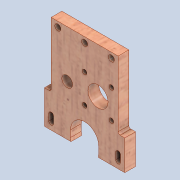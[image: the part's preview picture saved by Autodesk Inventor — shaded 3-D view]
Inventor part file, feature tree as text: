
AUTODESK INVENTOR PART (.ipt)
format: ipt  version: 2020 (Build 240168000, 168)  size: 326,656 bytes
history: native  units: mm
features: extrude x6, sketch x4, other x3, direct_edit x1, hole x1, fillet x1, reference x1, move_body x1
ambient origin geometry x8: Origin, YZ Plane, XZ Plane, XY Plane, X Axis, Y Axis, Z Axis, Center Point
bodies: Solid1 (feature_tree)
feature tree (18):
  extrude  "Extrusion1"  Depth=60.0mm
  extrude  "Extrusion4"  Depth=10.0mm TaperAngle=0.0deg
  extrude  "Extrusion5"  TaperAngle=0.0deg  [1 undecoded]
  extrude  "Extrusion6"  Depth=5.0mm
  extrude  "Extrusion7"  Depth=5.0mm
  extrude  "Extrusion8"  TaperAngle=0.0deg  [1 undecoded]
  direct_edit  "Direct Edit1"
  hole  "Hole1"  [1 undecoded]
  fillet  "Fillet1"  Radius=3.5mm
  sketch  "Sketch1"  dims[d0=60.0mm d1=65.0mm]
  sketch  "Sketch7"  dims[d2=8.0mm d3=0.0mm d11=10.0mm d12=0.0mm]
  reference  "Reference6"
  sketch  "Sketch8"  dims[d13=15.0mm d14=0.0mm d15=0.0mm]
  sketch  "Sketch9"  dims[d16=0.0mm d17=0.0mm d18=5.0mm d19=5.0mm d20=0.0mm d21=0.0mm d22=5.0mm d23=3.5mm d24=5.0mm d25=10.5mm d26=7.5mm d27=30.0mm d28=25.608627mm d29=20.0mm d31=21.5mm d33=3.5mm d35=8.0mm d36=17.0mm d37=27.469095mm d38=10.0mm d39=0.0mm d42=20.0mm d43=40.0mm d44=0.0mm d45=0.0mm d46=8.0mm d47=20.0mm d48=20.0mm d49=4.0mm d50=4.5mm d51=6.0mm d52=4.0mm d53=2.0mm d54=90.0deg d55=8.0mm d56=20.594885mm d57=1.5mm]
  parser-record x1  (decoder bookkeeping rows leaked as tree rows — omitted from the tree; the rows remain in map.json)
  other  "0005-00-00 Ansamblu_General.iam"
  other  "0005-10-002 Suport1 Seringa.ipt:8"
  move_body  "Move1"
note: 3 required parameter values undecoded (feature->parameter linkage not recoverable at this tier; creation-order binding heuristic only, values carry confidence <= 0.55)
note: 1 file-system path scrubbed to <path> (originals preserved in map.json)
